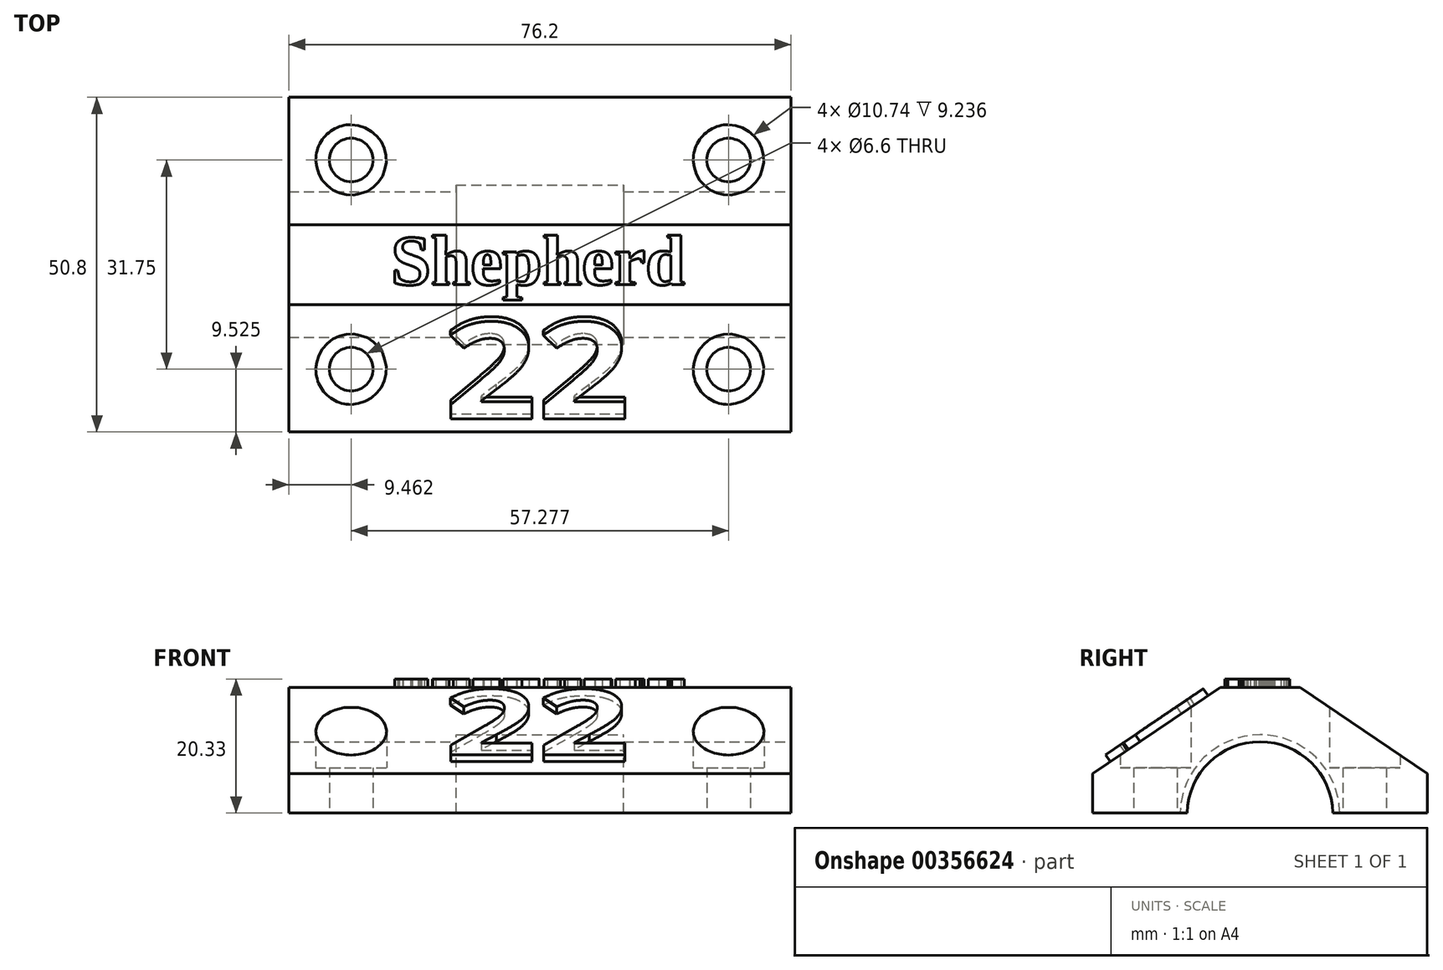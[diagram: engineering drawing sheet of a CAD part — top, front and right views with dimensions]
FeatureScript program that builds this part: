
annotation { "Feature Type Name" : "Feature", "Feature Type Description" : "" }
export const myFeature = defineFeature(function(context is Context, id is Id, definition is map)
    precondition{}
    {
        {
            var Q0;
            Q0=qCreatedBy(makeId("Front.planeOp"),FACE);
            var sketch = newSketch(context, id + "F0", { "sketchPlane" : qUnion([Q0])});
            skLineSegment(sketch, "E0.bottom", {"start": v(38.1, 9.53) * mm, "end": v(-38.1, 9.53) * mm});
            skLineSegment(sketch, "E0.top", {"start": v(38.1, -9.53) * mm, "end": v(-38.1, -9.53) * mm});
            skLineSegment(sketch, "E0.left", {"start": v(38.1, 9.53) * mm, "end": v(38.1, -9.52) * mm});
            skLineSegment(sketch, "E0.right", {"start": v(-38.1, 9.53) * mm, "end": v(-38.1, -9.53) * mm});
            skPoint(sketch, "E0.middle", {"position": v(0, 0) * mm});
            skSolve(sketch);
        }
        {
            var Q0;
            Q0=makeQuery(id+"F0.imprint","IMPRINT",FACE,{"disambiguationData":[TD([[makeQuery(id+"F0.imprint","IMPRINT",EDGE,{"derivedFrom":sQuery(id+"F0.wireOp",EDGE,"E0.bottom")}),1.0]])]});
            var Q1;
            Q1=qSketchRegion(id+"F2",true);
            extrude(context, id + "F1", {"entities" : qUnion([Q0, Q1]), "depth" : 50.8 * mm, "symmetric" : true});
        }
        {
            var Q0;
            Q0=makeQuery(id+"F1.opExtrude","SWEPT_FACE",FACE,{"disambiguationData":[OSD([sQuery(id+"F0.wireOp",EDGE,"E0.left")])]});
            var sketch = newSketch(context, id + "F2", { "sketchPlane" : qUnion([Q0])});
            skLineSegment(sketch, "E1.bottom", {"start": v(11.05, -9.52) * mm, "end": v(-11.05, -9.52) * mm});
            skPoint(sketch, "E1.middle", {"position": v(0, 0) * mm});
            skArc(sketch, "E2", {"start": v(11.05, -9.52) * mm, "mid": v(0, 1.27) * mm, "end": v(-11.05, -9.52) * mm});
            skLineSegment(sketch, "E3", {"start": v(-11.05, -9.52) * mm, "end": v(-12.13, -9.52) * mm});
            skLineSegment(sketch, "E4", {"start": v(11.05, -9.52) * mm, "end": v(12.1, -9.52) * mm});
            skLineSegment(sketch, "E5", {"start": v(0, 1.27) * mm, "end": v(0, 2.34) * mm});
            skArc(sketch, "E6", {"start": v(12.1, -9.52) * mm, "mid": v(-0.01, 2.34) * mm, "end": v(-12.13, -9.52) * mm});
            skArc(sketch, "E7", {"start": v(25.4, -9.52) * mm, "mid": v(0, 6.27) * mm, "end": v(-25.4, -9.52) * mm});
            skSolve(sketch);
        }
        {
            var Q0;
            {var subQ0=sQuery(id+"F2.wireOp",EDGE,"E1.bottom");Q0=makeQuery(id+"F2.imprint","IMPRINT",FACE,{"disambiguationData":[TD([[makeQuery(id+"F2.imprint","IMPRINT",EDGE,{"derivedFrom":subQ0}),1.0]])]});}
            extrude(context, id + "F3", {"entities" : qUnion([Q0]), "operationType" : NewBodyOperationType.REMOVE, "oppositeDirection" : true, "depth" : 76.2 * mm});
        }
        {
            var Q0;
            {var subQ0=sQuery(id+"F2.wireOp",EDGE,"E3");Q0=makeQuery(id+"F2.imprint","IMPRINT",FACE,{"disambiguationData":[TD([[makeQuery(id+"F2.imprint","IMPRINT",EDGE,{"derivedFrom":subQ0}),1.0]])]});}
            var Q1;
            {var subQ0=sQuery(id+"F2.wireOp",EDGE,"E4");Q1=makeQuery(id+"F2.imprint","IMPRINT",FACE,{"disambiguationData":[TD([[makeQuery(id+"F2.imprint","IMPRINT",EDGE,{"derivedFrom":subQ0}),1.0]])]});}
            var Q2;
            {var subQ0=sQuery(id+"F2.wireOp",EDGE,"E1.bottom");Q2=makeQuery(id+"F2.imprint","IMPRINT",FACE,{"disambiguationData":[TD([[makeQuery(id+"F2.imprint","IMPRINT",EDGE,{"derivedFrom":subQ0}),1.0]])]});}
            extrude(context, id + "F4", {"entities" : qUnion([Q0, Q1, Q2]), "operationType" : NewBodyOperationType.REMOVE, "oppositeDirection" : true, "depth" : 50.8 * mm, "hasSecondDirection" : true, "secondDirectionOppositeDirection" : true, "secondDirectionDepth" : 25.4 * mm});
        }
        {
            var Q0;
            Q0=makeQuery(id+"F1.opExtrude","SWEPT_FACE",FACE,{"disambiguationData":[OSD([sQuery(id+"F0.wireOp",EDGE,"E0.bottom")])]});
            var sketch = newSketch(context, id + "F5", { "sketchPlane" : qUnion([Q0])});
            skLineSegment(sketch, "E8.bottom", {"start": v(-28.64, -15.87) * mm, "end": v(28.64, -15.87) * mm});
            skLineSegment(sketch, "E8.top", {"start": v(-28.64, 15.88) * mm, "end": v(28.64, 15.88) * mm});
            skLineSegment(sketch, "E8.left", {"start": v(-28.64, -15.87) * mm, "end": v(-28.64, 15.88) * mm});
            skLineSegment(sketch, "E8.right", {"start": v(28.64, -15.87) * mm, "end": v(28.64, 15.88) * mm});
            skPoint(sketch, "E8.middle", {"position": v(0, 0) * mm});
            skSolve(sketch);
        }
        {
            var Q0;
            Q0=sQuery(id+"F5.wireOp",VERTEX,"E8.left.end");
            var Q1;
            Q1=sQuery(id+"F5.wireOp",VERTEX,"E8.left.start");
            var Q2;
            Q2=sQuery(id+"F5.wireOp",VERTEX,"E8.right.start");
            var Q3;
            Q3=sQuery(id+"F5.wireOp",VERTEX,"E8.right.end");
            var Q4;
            Q4=makeQuery(id+"F1.opExtrude","SWEPT_BODY",BODY,{"disambiguationData":[OSD([sQuery(id+"F0.wireOp",EDGE,"E0.bottom"),sQuery(id+"F0.wireOp",EDGE,"E0.top"),sQuery(id+"F0.wireOp",EDGE,"E0.left"),sQuery(id+"F0.wireOp",EDGE,"E0.right")])]});
            hole(context, id + "F6", {"style" : HoleStyle.C_BORE, "endStyle" : HoleEndStyle.THROUGH, "holeDiameter" : 6.6 * mm, "cBoreDiameter" : 10.74 * mm, "cBoreDepth" : 12.2 * mm, "isTappedThrough" : true, "tappedDepth" : 12.7 * mm, "tapClearance" : 3, "locations" : qUnion([Q0, Q1, Q2, Q3]), "scope" : qUnion([Q4])});
        }
        {
            var Q0;
            Q0=makeQuery(id+"F1.opExtrude","SWEPT_FACE",FACE,{"disambiguationData":[OSD([sQuery(id+"F0.wireOp",EDGE,"E0.right")])]});
            var sketch = newSketch(context, id + "F7", { "sketchPlane" : qUnion([Q0])});
            skLineSegment(sketch, "E9", {"start": v(-25.4, -9.53) * mm, "end": v(-25.4, -3.56) * mm});
            skLineSegment(sketch, "E10", {"start": v(-25.4, -3.56) * mm, "end": v(-6.06, 9.52) * mm});
            skLineSegment(sketch, "E11.MirrorCS", {"start": v(25.4, -3.56) * mm, "end": v(6.06, 9.52) * mm});
            skSolve(sketch);
        }
        {
            var Q0;
            Q0 = qSketchRegion(id + "F7", true);
            var Q1;
            {var subQ0=sQuery(id+"F7.wireOp",EDGE,"E10");Q1=makeQuery(id+"F7.imprint","IMPRINT",FACE,{"disambiguationData":[TD([[makeQuery(id+"F7.imprint","IMPRINT",EDGE,{"derivedFrom":subQ0}),1.0]])]});}
            var Q2;
            {var subQ0=sQuery(id+"F7.wireOp",EDGE,"E11.MirrorCS");Q2=makeQuery(id+"F7.imprint","IMPRINT",FACE,{"disambiguationData":[TD([[makeQuery(id+"F7.imprint","IMPRINT",EDGE,{"derivedFrom":subQ0}),-1.0]])]});}
            extrude(context, id + "F8", {"entities" : qUnion([Q0, Q1, Q2]), "operationType" : NewBodyOperationType.REMOVE, "oppositeDirection" : true, "depth" : 76.2 * mm});
        }
        {
            var Q0;
            Q0=makeQuery(id+"F1.opExtrude","SWEPT_FACE",FACE,{"disambiguationData":[OSD([sQuery(id+"F0.wireOp",EDGE,"E0.bottom")])]});
            var sketch = newSketch(context, id + "F9", { "sketchPlane" : qUnion([Q0])});
            skText(sketch, "E12", { "text": "Shepherd", "fontName": "Tinos-Bold.ttf"});
            const initialGuessF9  = {"E12": [-0.0226, -0.00306, 1, 0, 0.00782]};
            skSetInitialGuess(sketch, initialGuessF9);
            skSolve(sketch);
        }
        {
            var Q0;
            Q0 = qSketchRegion(id + "F9", true);
            extrude(context, id + "F10", {"entities" : qUnion([Q0]), "operationType" : NewBodyOperationType.ADD, "depth" : 1.27 * mm});
        }
        {
            var Q0;
            Q0=makeQuery(id+"F8.boolean.opBoolean","COPY",FACE,{"derivedFrom":makeQuery(id+"F8.opExtrude","SWEPT_FACE",FACE,{"disambiguationData":[OSD([sQuery(id+"F7.wireOp",EDGE,"E11.MirrorCS")])]})});
            var sketch = newSketch(context, id + "F11", { "sketchPlane" : qUnion([Q0])});
            skText(sketch, "E13", { "text": "22", "fontName": "OpenSans-Bold.ttf"});
            const initialGuessF11  = {"E13": [-0.0145, -0.01979, 1, 0, 0.01778]};
            skSetInitialGuess(sketch, initialGuessF11);
            skSolve(sketch);
        }
        {
            var Q0;
            Q0=makeQuery(id+"F11.imprint","IMPRINT",FACE,{"disambiguationData":[TD([[makeQuery(id+"F11.imprint","IMPRINT",EDGE,{"derivedFrom":sQuery(id+"F11.wireOp",EDGE,"E13.sketch_text.stroke-24")}),-1.0]])]});
            var Q1;
            Q1=makeQuery(id+"F11.imprint","IMPRINT",FACE,{"disambiguationData":[TD([[makeQuery(id+"F11.imprint","IMPRINT",EDGE,{"derivedFrom":sQuery(id+"F11.wireOp",EDGE,"E13.sketch_text.stroke-0")}),-1.0]])]});
            extrude(context, id + "F12", {"entities" : qUnion([Q0, Q1]), "operationType" : NewBodyOperationType.ADD, "depth" : 1.27 * mm});
        }
    });
